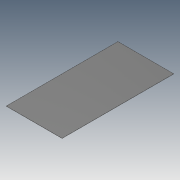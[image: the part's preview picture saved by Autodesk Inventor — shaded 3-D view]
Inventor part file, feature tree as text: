
AUTODESK INVENTOR PART (.ipt)
format: ipt  version: 2020 (Build 240168000, 168)  size: 77,824 bytes
history: native  units: mm
features: other x1, extrude x1, sketch x1
ambient origin geometry x8: Origin, YZ Plane, XZ Plane, XY Plane, X Axis, Y Axis, Z Axis, Center Point
bodies: Body1 (feature_tree)
feature tree (3):
  other  "ソリッド1"
  extrude  "押し出し1"  Depth=1500.0mm
  sketch  "スケッチ1"
